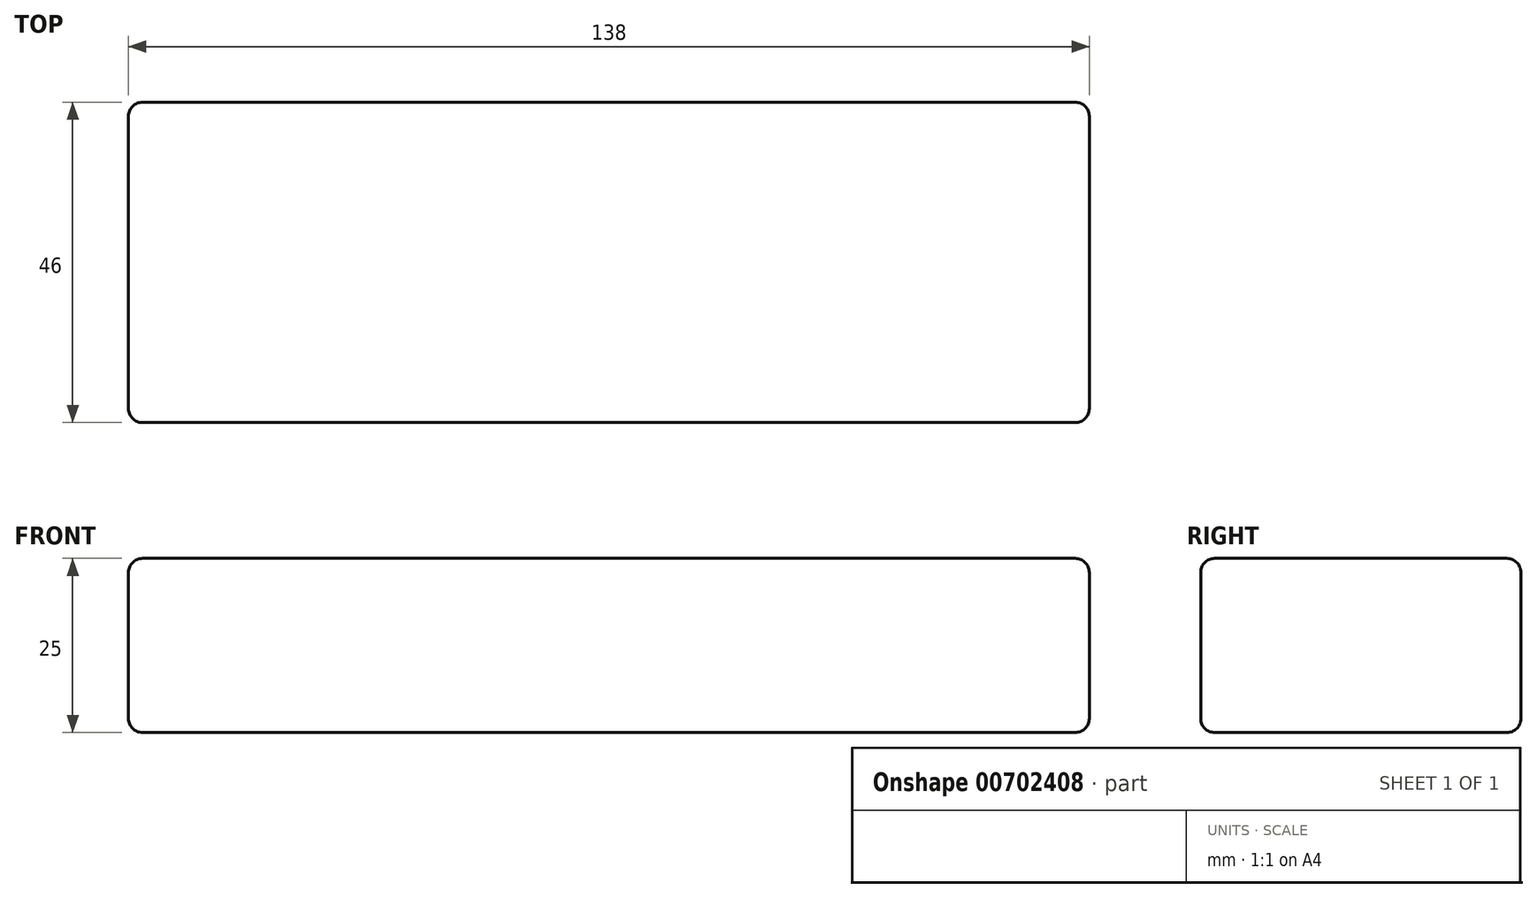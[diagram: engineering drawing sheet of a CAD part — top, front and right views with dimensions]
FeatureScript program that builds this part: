
annotation { "Feature Type Name" : "Feature", "Feature Type Description" : "" }
export const myFeature = defineFeature(function(context is Context, id is Id, definition is map)
    precondition{}
    {
        {
            var Q0;
            Q0=qCreatedBy(makeId("Top.planeOp"),FACE);
            var sketch = newSketch(context, id + "F0", { "sketchPlane" : qUnion([Q0])});
            skLineSegment(sketch, "E0.bottom", {"start": v(69, 23) * mm, "end": v(-69, 23) * mm});
            skLineSegment(sketch, "E0.top", {"start": v(69, -23) * mm, "end": v(-69, -23) * mm});
            skLineSegment(sketch, "E0.left", {"start": v(69, 23) * mm, "end": v(69, -23) * mm});
            skLineSegment(sketch, "E0.right", {"start": v(-69, 23) * mm, "end": v(-69, -23) * mm});
            skPoint(sketch, "E0.middle", {"position": v(0, 0) * mm});
            skSolve(sketch);
        }
        {
            var Q0;
            Q0=makeQuery(id+"F0.imprint","IMPRINT",FACE,{"disambiguationData":[TD([[makeQuery(id+"F0.imprint","IMPRINT",EDGE,{"derivedFrom":sQuery(id+"F0.wireOp",EDGE,"E0.bottom")}),1.0]])]});
            extrude(context, id + "F1", {"entities" : qUnion([Q0]), "depth" : 25 * mm, "offsetDistance" : 25 * mm});
        }
        {
            var Q0;
            Q0=makeQuery(id+"F1.opExtrude","CAP_FACE",FACE,{"disambiguationData":[OSD([sQuery(id+"F0.wireOp",EDGE,"E0.bottom"),sQuery(id+"F0.wireOp",EDGE,"E0.top"),sQuery(id+"F0.wireOp",EDGE,"E0.left"),sQuery(id+"F0.wireOp",EDGE,"E0.right")])],"isStart":false});
            var Q1;
            Q1=makeQuery(id+"F1.opExtrude","SWEPT_FACE",FACE,{"disambiguationData":[OSD([sQuery(id+"F0.wireOp",EDGE,"E0.top")])]});
            var Q2;
            Q2=makeQuery(id+"F1.opExtrude","CAP_EDGE",EDGE,{"disambiguationData":[OSD([sQuery(id+"F0.wireOp",EDGE,"E0.left")])],"isStart":true});
            var Q3;
            Q3=makeQuery(id+"F1.opExtrude","CAP_FACE",FACE,{"disambiguationData":[OSD([sQuery(id+"F0.wireOp",EDGE,"E0.bottom"),sQuery(id+"F0.wireOp",EDGE,"E0.top"),sQuery(id+"F0.wireOp",EDGE,"E0.left"),sQuery(id+"F0.wireOp",EDGE,"E0.right")])],"isStart":true});
            var Q4;
            Q4=makeQuery(id+"F1.opExtrude","SWEPT_FACE",FACE,{"disambiguationData":[OSD([sQuery(id+"F0.wireOp",EDGE,"E0.bottom")])]});
            var Q5;
            Q5=makeQuery(id+"F1.opExtrude","SWEPT_FACE",FACE,{"disambiguationData":[OSD([sQuery(id+"F0.wireOp",EDGE,"E0.right")])]});
            fillet(context, id + "F2", {"entities" : qUnion([Q0, Q1, Q2, Q3, Q4, Q5]), "radius" : 2 * mm, "tangentPropagation" : true, "allowEdgeOverflow" : false});
        }
    });
